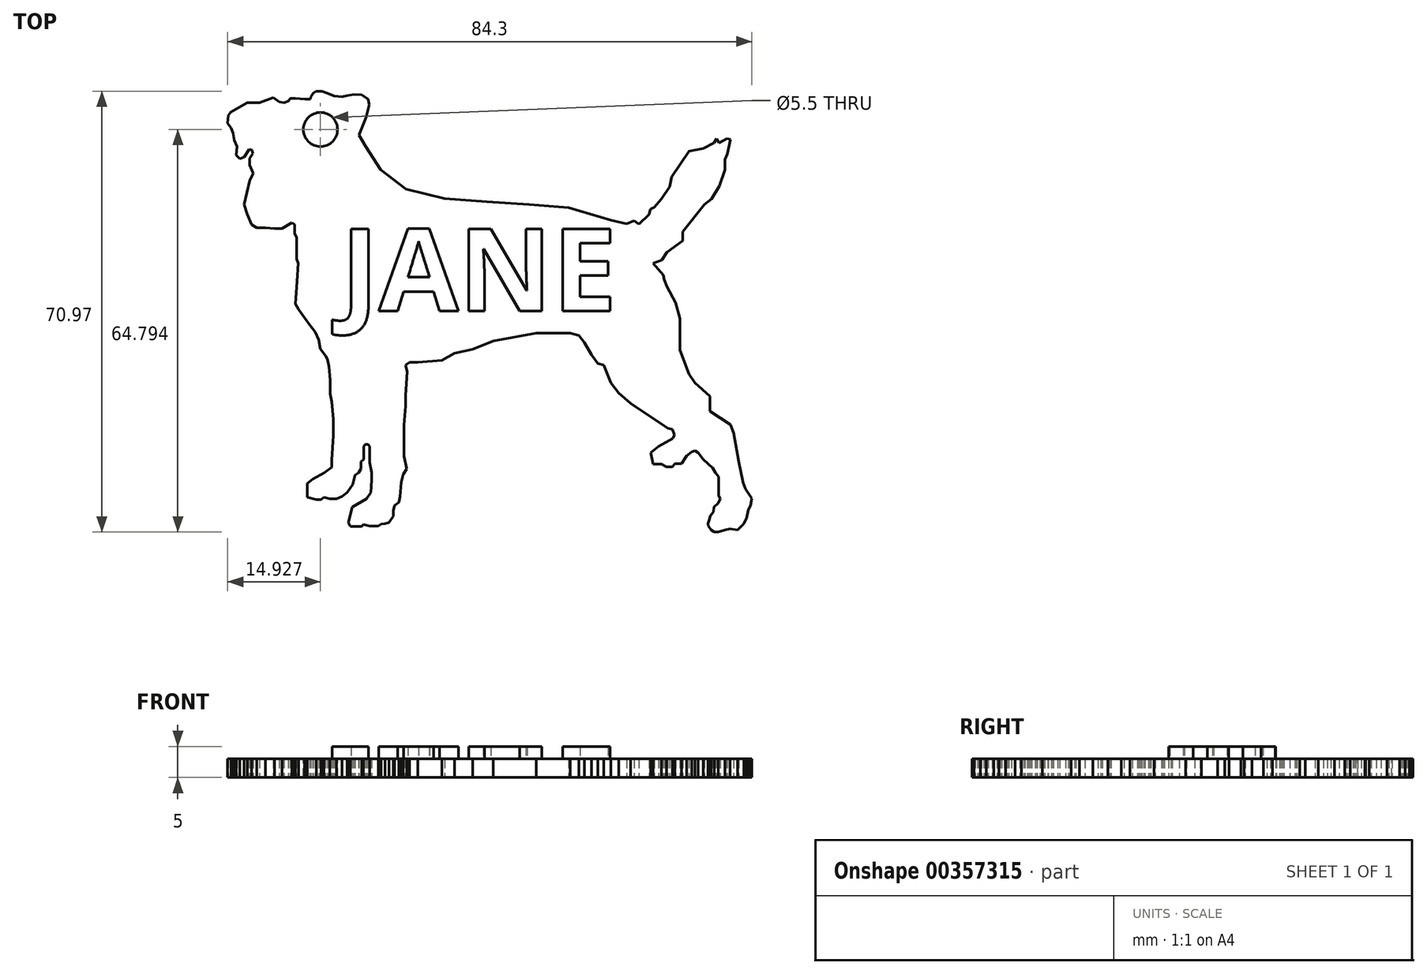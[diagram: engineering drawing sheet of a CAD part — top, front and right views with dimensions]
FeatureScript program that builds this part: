
annotation { "Feature Type Name" : "Feature", "Feature Type Description" : "" }
export const myFeature = defineFeature(function(context is Context, id is Id, definition is map)
    precondition{}
    {
        {
            var Q0;
            Q0=qCreatedBy(makeId("Top.planeOp"),FACE);
            var sketch = newSketch(context, id + "F0", { "sketchPlane" : qUnion([Q0])});
            skLineSegment(sketch, "E0", {"start": v(-3.64, 1.42) * mm, "end": v(-2.43, 1.25) * mm});
            skLineSegment(sketch, "E1", {"start": v(-2.43, 1.25) * mm, "end": v(-1.42, 2.22) * mm});
            skLineSegment(sketch, "E2", {"start": v(-1.42, 2.22) * mm, "end": v(-0.94, 3.22) * mm});
            skLineSegment(sketch, "E3", {"start": v(-0.94, 3.22) * mm, "end": v(-0.7, 4.4) * mm});
            skLineSegment(sketch, "E4", {"start": v(-0.7, 4.4) * mm, "end": v(-0.36, 5.26) * mm});
            skLineSegment(sketch, "E5", {"start": v(-0.36, 5.26) * mm, "end": v(-0.15, 6.3) * mm});
            skLineSegment(sketch, "E6", {"start": v(-0.15, 6.3) * mm, "end": v(-1.13, 7.85) * mm});
            skLineSegment(sketch, "E7", {"start": v(-1.13, 7.85) * mm, "end": v(-1.54, 8.84) * mm});
            skLineSegment(sketch, "E8", {"start": v(-1.54, 8.84) * mm, "end": v(-2.22, 12.2) * mm});
            skLineSegment(sketch, "E9", {"start": v(-2.22, 12.2) * mm, "end": v(-3.06, 16.88) * mm});
            skLineSegment(sketch, "E10", {"start": v(-3.06, 16.88) * mm, "end": v(-3.59, 18.18) * mm});
            skLineSegment(sketch, "E11", {"start": v(-3.59, 18.18) * mm, "end": v(-6.88, 20.38) * mm});
            skLineSegment(sketch, "E12", {"start": v(-6.88, 20.38) * mm, "end": v(-6.88, 22.74) * mm});
            skLineSegment(sketch, "E13", {"start": v(-6.88, 22.74) * mm, "end": v(-9.3, 24.95) * mm});
            skLineSegment(sketch, "E14", {"start": v(-9.3, 24.95) * mm, "end": v(-10.24, 26.3) * mm});
            skLineSegment(sketch, "E15", {"start": v(-10.24, 26.3) * mm, "end": v(-11.68, 30.22) * mm});
            skLineSegment(sketch, "E16", {"start": v(-11.68, 30.22) * mm, "end": v(-11.68, 35.25) * mm});
            skLineSegment(sketch, "E17", {"start": v(-11.68, 35.25) * mm, "end": v(-12.4, 37.82) * mm});
            skLineSegment(sketch, "E18", {"start": v(-12.4, 37.82) * mm, "end": v(-13.77, 40.43) * mm});
            skLineSegment(sketch, "E19", {"start": v(-13.77, 40.43) * mm, "end": v(-14.23, 41.56) * mm});
            skLineSegment(sketch, "E20", {"start": v(-14.23, 41.56) * mm, "end": v(-14.35, 42.25) * mm});
            skLineSegment(sketch, "E21", {"start": v(-14.35, 42.25) * mm, "end": v(-15.99, 44.15) * mm});
            skLineSegment(sketch, "E22", {"start": v(-15.99, 44.15) * mm, "end": v(-14.65, 44.64) * mm});
            skLineSegment(sketch, "E23", {"start": v(-14.65, 44.64) * mm, "end": v(-13.78, 45.95) * mm});
            skLineSegment(sketch, "E24", {"start": v(-13.78, 45.95) * mm, "end": v(-11.25, 47.77) * mm});
            skLineSegment(sketch, "E25", {"start": v(-11.25, 47.77) * mm, "end": v(-11.25, 49.24) * mm});
            skLineSegment(sketch, "E26", {"start": v(-11.25, 49.24) * mm, "end": v(-7.8, 53.6) * mm});
            skLineSegment(sketch, "E27", {"start": v(-7.8, 53.6) * mm, "end": v(-6.61, 54.52) * mm});
            skLineSegment(sketch, "E28", {"start": v(-6.61, 54.52) * mm, "end": v(-5.38, 56.64) * mm});
            skLineSegment(sketch, "E29", {"start": v(-5.38, 56.64) * mm, "end": v(-4.49, 59.24) * mm});
            skLineSegment(sketch, "E30", {"start": v(-4.49, 59.24) * mm, "end": v(-4.49, 60.88) * mm});
            skLineSegment(sketch, "E31", {"start": v(-4.49, 60.88) * mm, "end": v(-4.1, 61.74) * mm});
            skLineSegment(sketch, "E32", {"start": v(-4.1, 61.74) * mm, "end": v(-3.56, 64.1) * mm});
            skLineSegment(sketch, "E33", {"start": v(-3.56, 64.1) * mm, "end": v(-4.14, 64.23) * mm});
            skLineSegment(sketch, "E34", {"start": v(-4.14, 64.23) * mm, "end": v(-5.41, 63.5) * mm});
            skLineSegment(sketch, "E35", {"start": v(-5.41, 63.5) * mm, "end": v(-5.8, 64.2) * mm});
            skLineSegment(sketch, "E36", {"start": v(-5.8, 64.2) * mm, "end": v(-6.26, 63.5) * mm});
            skLineSegment(sketch, "E37", {"start": v(-6.26, 63.5) * mm, "end": v(-7.98, 62.65) * mm});
            skLineSegment(sketch, "E38", {"start": v(-7.98, 62.65) * mm, "end": v(-10.24, 62.2) * mm});
            skLineSegment(sketch, "E39", {"start": v(-10.24, 62.2) * mm, "end": v(-12.26, 59.17) * mm});
            skLineSegment(sketch, "E40", {"start": v(-12.26, 59.17) * mm, "end": v(-13, 58.05) * mm});
            skLineSegment(sketch, "E41", {"start": v(-13, 58.05) * mm, "end": v(-13.32, 56.49) * mm});
            skLineSegment(sketch, "E42", {"start": v(-13.32, 56.49) * mm, "end": v(-14.65, 54.5) * mm});
            skLineSegment(sketch, "E43", {"start": v(-14.65, 54.5) * mm, "end": v(-15.82, 53.16) * mm});
            skLineSegment(sketch, "E44", {"start": v(-15.82, 53.16) * mm, "end": v(-16.47, 52.9) * mm});
            skLineSegment(sketch, "E45", {"start": v(-16.47, 52.9) * mm, "end": v(-16.67, 52.06) * mm});
            skLineSegment(sketch, "E46", {"start": v(-16.67, 52.06) * mm, "end": v(-18.33, 50.48) * mm});
            skLineSegment(sketch, "E47", {"start": v(-18.33, 50.48) * mm, "end": v(-19.1, 51) * mm});
            skLineSegment(sketch, "E48", {"start": v(-19.1, 51) * mm, "end": v(-20.28, 50.51) * mm});
            skLineSegment(sketch, "E49", {"start": v(-20.28, 50.51) * mm, "end": v(-22.75, 51.11) * mm});
            skLineSegment(sketch, "E50", {"start": v(-22.75, 51.11) * mm, "end": v(-29.59, 53.13) * mm});
            skLineSegment(sketch, "E51", {"start": v(-29.59, 53.13) * mm, "end": v(-35.94, 53.6) * mm});
            skLineSegment(sketch, "E52", {"start": v(-35.94, 53.6) * mm, "end": v(-42.74, 54.08) * mm});
            skLineSegment(sketch, "E53", {"start": v(-42.74, 54.08) * mm, "end": v(-49.55, 54.6) * mm});
            skLineSegment(sketch, "E54", {"start": v(-49.55, 54.6) * mm, "end": v(-55.76, 56.1) * mm});
            skLineSegment(sketch, "E55", {"start": v(-55.76, 56.1) * mm, "end": v(-59.84, 59.24) * mm});
            skLineSegment(sketch, "E56", {"start": v(-59.84, 59.24) * mm, "end": v(-62.23, 62.97) * mm});
            skLineSegment(sketch, "E57", {"start": v(-62.23, 62.97) * mm, "end": v(-63.35, 64.79) * mm});
            skLineSegment(sketch, "E58", {"start": v(-63.35, 64.79) * mm, "end": v(-62.2, 67.64) * mm});
            skLineSegment(sketch, "E59", {"start": v(-62.2, 67.64) * mm, "end": v(-61.7, 69.7) * mm});
            skLineSegment(sketch, "E60", {"start": v(-61.7, 69.7) * mm, "end": v(-61.87, 70.6) * mm});
            skLineSegment(sketch, "E61", {"start": v(-61.87, 70.6) * mm, "end": v(-62.86, 71.27) * mm});
            skLineSegment(sketch, "E62", {"start": v(-62.86, 71.27) * mm, "end": v(-64.08, 71.35) * mm});
            skLineSegment(sketch, "E63", {"start": v(-64.08, 71.35) * mm, "end": v(-65.22, 71.15) * mm});
            skLineSegment(sketch, "E64", {"start": v(-65.22, 71.15) * mm, "end": v(-66.05, 70.98) * mm});
            skLineSegment(sketch, "E65", {"start": v(-66.05, 70.98) * mm, "end": v(-67.32, 71.07) * mm});
            skLineSegment(sketch, "E66", {"start": v(-67.32, 71.07) * mm, "end": v(-68.4, 71.56) * mm});
            skLineSegment(sketch, "E67", {"start": v(-68.4, 71.56) * mm, "end": v(-69.29, 71.87) * mm});
            skLineSegment(sketch, "E68", {"start": v(-69.29, 71.87) * mm, "end": v(-70.27, 71.87) * mm});
            skLineSegment(sketch, "E69", {"start": v(-70.27, 71.87) * mm, "end": v(-70.7, 71.5) * mm});
            skLineSegment(sketch, "E70", {"start": v(-70.7, 71.5) * mm, "end": v(-71.06, 70.98) * mm});
            skLineSegment(sketch, "E71", {"start": v(-71.06, 70.98) * mm, "end": v(-71.15, 70.6) * mm});
            skLineSegment(sketch, "E72", {"start": v(-71.15, 70.6) * mm, "end": v(-72.04, 70.6) * mm});
            skLineSegment(sketch, "E73", {"start": v(-72.04, 70.6) * mm, "end": v(-73.58, 70.72) * mm});
            skLineSegment(sketch, "E74", {"start": v(-73.58, 70.72) * mm, "end": v(-74.4, 70.72) * mm});
            skLineSegment(sketch, "E75", {"start": v(-74.4, 70.72) * mm, "end": v(-74.71, 70.26) * mm});
            skLineSegment(sketch, "E76", {"start": v(-74.71, 70.26) * mm, "end": v(-75.4, 69.99) * mm});
            skLineSegment(sketch, "E77", {"start": v(-75.4, 69.99) * mm, "end": v(-76.13, 70.17) * mm});
            skLineSegment(sketch, "E78", {"start": v(-76.13, 70.17) * mm, "end": v(-77.12, 70.82) * mm});
            skLineSegment(sketch, "E79", {"start": v(-77.12, 70.82) * mm, "end": v(-78.44, 70.34) * mm});
            skLineSegment(sketch, "E80", {"start": v(-78.44, 70.34) * mm, "end": v(-79.36, 70) * mm});
            skLineSegment(sketch, "E81", {"start": v(-79.36, 70) * mm, "end": v(-81.32, 70) * mm});
            skLineSegment(sketch, "E82", {"start": v(-81.32, 70) * mm, "end": v(-83.98, 68.5) * mm});
            skLineSegment(sketch, "E83", {"start": v(-83.98, 68.5) * mm, "end": v(-84.32, 67.99) * mm});
            skLineSegment(sketch, "E84", {"start": v(-84.32, 67.99) * mm, "end": v(-84.45, 66.71) * mm});
            skLineSegment(sketch, "E85", {"start": v(-84.45, 66.71) * mm, "end": v(-83.92, 65.94) * mm});
            skLineSegment(sketch, "E86", {"start": v(-83.92, 65.94) * mm, "end": v(-83.61, 65.1) * mm});
            skLineSegment(sketch, "E87", {"start": v(-83.61, 65.1) * mm, "end": v(-83.39, 64) * mm});
            skLineSegment(sketch, "E88", {"start": v(-83.39, 64) * mm, "end": v(-82.97, 62.97) * mm});
            skLineSegment(sketch, "E89", {"start": v(-82.97, 62.97) * mm, "end": v(-83.07, 61.56) * mm});
            skLineSegment(sketch, "E90", {"start": v(-83.07, 61.56) * mm, "end": v(-82.5, 60.97) * mm});
            skLineSegment(sketch, "E91", {"start": v(-82.5, 60.97) * mm, "end": v(-81.81, 61.24) * mm});
            skLineSegment(sketch, "E92", {"start": v(-81.81, 61.24) * mm, "end": v(-81.33, 61.97) * mm});
            skLineSegment(sketch, "E93", {"start": v(-81.33, 61.97) * mm, "end": v(-80.97, 62.52) * mm});
            skLineSegment(sketch, "E94", {"start": v(-80.97, 62.52) * mm, "end": v(-80.5, 62.4) * mm});
            skLineSegment(sketch, "E95", {"start": v(-80.5, 62.4) * mm, "end": v(-80.38, 61.8) * mm});
            skLineSegment(sketch, "E96", {"start": v(-80.38, 61.8) * mm, "end": v(-80.9, 61.03) * mm});
            skLineSegment(sketch, "E97", {"start": v(-80.9, 61.03) * mm, "end": v(-80.9, 59.97) * mm});
            skLineSegment(sketch, "E98", {"start": v(-80.9, 59.97) * mm, "end": v(-80.36, 58.63) * mm});
            skLineSegment(sketch, "E99", {"start": v(-80.36, 58.63) * mm, "end": v(-80.9, 57.45) * mm});
            skLineSegment(sketch, "E100", {"start": v(-80.9, 57.45) * mm, "end": v(-81.32, 55.75) * mm});
            skLineSegment(sketch, "E101", {"start": v(-81.32, 55.75) * mm, "end": v(-81.83, 53.6) * mm});
            skLineSegment(sketch, "E102", {"start": v(-81.83, 53.6) * mm, "end": v(-81.27, 52.06) * mm});
            skLineSegment(sketch, "E103", {"start": v(-81.27, 52.06) * mm, "end": v(-80.6, 50.4) * mm});
            skLineSegment(sketch, "E104", {"start": v(-80.6, 50.4) * mm, "end": v(-79.8, 49.86) * mm});
            skLineSegment(sketch, "E105", {"start": v(-79.8, 49.86) * mm, "end": v(-78.37, 49.86) * mm});
            skLineSegment(sketch, "E106", {"start": v(-78.37, 49.86) * mm, "end": v(-76.93, 49.76) * mm});
            skLineSegment(sketch, "E107", {"start": v(-76.93, 49.76) * mm, "end": v(-75.74, 49.76) * mm});
            skLineSegment(sketch, "E108", {"start": v(-75.74, 49.76) * mm, "end": v(-74.9, 50.24) * mm});
            skLineSegment(sketch, "E109", {"start": v(-74.9, 50.24) * mm, "end": v(-74.11, 50.68) * mm});
            skLineSegment(sketch, "E110", {"start": v(-74.11, 50.68) * mm, "end": v(-73.68, 50.4) * mm});
            skLineSegment(sketch, "E111", {"start": v(-73.68, 50.4) * mm, "end": v(-73.68, 48.9) * mm});
            skLineSegment(sketch, "E112", {"start": v(-73.68, 48.9) * mm, "end": v(-73.38, 48.38) * mm});
            skLineSegment(sketch, "E113", {"start": v(-73.38, 48.38) * mm, "end": v(-73.38, 44.89) * mm});
            skLineSegment(sketch, "E114", {"start": v(-73.38, 44.89) * mm, "end": v(-73.09, 44.17) * mm});
            skLineSegment(sketch, "E115", {"start": v(-73.09, 44.17) * mm, "end": v(-73.3, 41.23) * mm});
            skLineSegment(sketch, "E116", {"start": v(-73.3, 41.23) * mm, "end": v(-73.57, 37.63) * mm});
            skLineSegment(sketch, "E117", {"start": v(-73.57, 37.63) * mm, "end": v(-73.05, 36.72) * mm});
            skLineSegment(sketch, "E118", {"start": v(-73.05, 36.72) * mm, "end": v(-72.1, 35.37) * mm});
            skLineSegment(sketch, "E119", {"start": v(-72.1, 35.37) * mm, "end": v(-71.25, 34.24) * mm});
            skLineSegment(sketch, "E120", {"start": v(-71.25, 34.24) * mm, "end": v(-70.35, 33.14) * mm});
            skLineSegment(sketch, "E121", {"start": v(-70.35, 33.14) * mm, "end": v(-69.83, 31.85) * mm});
            skLineSegment(sketch, "E122", {"start": v(-69.83, 31.85) * mm, "end": v(-69.53, 30.4) * mm});
            skLineSegment(sketch, "E123", {"start": v(-69.53, 30.4) * mm, "end": v(-68.74, 29.32) * mm});
            skLineSegment(sketch, "E124", {"start": v(-68.74, 29.32) * mm, "end": v(-68.4, 28.71) * mm});
            skLineSegment(sketch, "E125", {"start": v(-68.4, 28.71) * mm, "end": v(-68.15, 27.5) * mm});
            skLineSegment(sketch, "E126", {"start": v(-68.15, 27.5) * mm, "end": v(-67.95, 25.36) * mm});
            skLineSegment(sketch, "E127", {"start": v(-67.95, 25.36) * mm, "end": v(-67.95, 23.15) * mm});
            skLineSegment(sketch, "E128", {"start": v(-67.95, 23.15) * mm, "end": v(-67.69, 21.87) * mm});
            skLineSegment(sketch, "E129", {"start": v(-67.69, 21.87) * mm, "end": v(-67.47, 19.06) * mm});
            skLineSegment(sketch, "E130", {"start": v(-67.47, 19.06) * mm, "end": v(-67.47, 16.4) * mm});
            skLineSegment(sketch, "E131", {"start": v(-67.47, 16.4) * mm, "end": v(-67.59, 14.67) * mm});
            skLineSegment(sketch, "E132", {"start": v(-67.59, 14.67) * mm, "end": v(-67.74, 12.53) * mm});
            skLineSegment(sketch, "E133", {"start": v(-67.74, 12.53) * mm, "end": v(-67.74, 11.33) * mm});
            skLineSegment(sketch, "E134", {"start": v(-67.74, 11.33) * mm, "end": v(-68.93, 10.43) * mm});
            skLineSegment(sketch, "E135", {"start": v(-68.93, 10.43) * mm, "end": v(-70.73, 9.4) * mm});
            skLineSegment(sketch, "E136", {"start": v(-70.73, 9.4) * mm, "end": v(-71.64, 8.72) * mm});
            skLineSegment(sketch, "E137", {"start": v(-71.64, 8.72) * mm, "end": v(-71.64, 6.5) * mm});
            skLineSegment(sketch, "E138", {"start": v(-71.64, 6.5) * mm, "end": v(-70.19, 6.14) * mm});
            skLineSegment(sketch, "E139", {"start": v(-70.19, 6.14) * mm, "end": v(-69.45, 6.14) * mm});
            skLineSegment(sketch, "E140", {"start": v(-69.45, 6.14) * mm, "end": v(-69, 6.49) * mm});
            skLineSegment(sketch, "E141", {"start": v(-69, 6.49) * mm, "end": v(-68.05, 6.26) * mm});
            skLineSegment(sketch, "E142", {"start": v(-68.05, 6.26) * mm, "end": v(-67.59, 6.26) * mm});
            skLineSegment(sketch, "E143", {"start": v(-67.59, 6.26) * mm, "end": v(-66.97, 6.26) * mm});
            skLineSegment(sketch, "E144", {"start": v(-66.97, 6.26) * mm, "end": v(-66.05, 6.63) * mm});
            skLineSegment(sketch, "E145", {"start": v(-66.05, 6.63) * mm, "end": v(-65.23, 7.24) * mm});
            skLineSegment(sketch, "E146", {"start": v(-65.23, 7.24) * mm, "end": v(-64.83, 7.85) * mm});
            skLineSegment(sketch, "E147", {"start": v(-64.83, 7.85) * mm, "end": v(-64.35, 8.57) * mm});
            skLineSegment(sketch, "E148", {"start": v(-64.35, 8.57) * mm, "end": v(-64, 10.04) * mm});
            skLineSegment(sketch, "E149", {"start": v(-64, 10.04) * mm, "end": v(-63.42, 10.48) * mm});
            skLineSegment(sketch, "E150", {"start": v(-63.42, 10.48) * mm, "end": v(-63.03, 11.07) * mm});
            skLineSegment(sketch, "E151", {"start": v(-63.03, 11.07) * mm, "end": v(-63.03, 12.23) * mm});
            skLineSegment(sketch, "E152", {"start": v(-63.03, 12.23) * mm, "end": v(-62.56, 12.57) * mm});
            skLineSegment(sketch, "E153", {"start": v(-62.56, 12.57) * mm, "end": v(-62.56, 14.67) * mm});
            skLineSegment(sketch, "E154", {"start": v(-62.56, 14.67) * mm, "end": v(-62.33, 15.02) * mm});
            skLineSegment(sketch, "E155", {"start": v(-62.33, 15.02) * mm, "end": v(-61.87, 15.02) * mm});
            skLineSegment(sketch, "E156", {"start": v(-61.87, 15.02) * mm, "end": v(-61.6, 14.67) * mm});
            skLineSegment(sketch, "E157", {"start": v(-61.6, 14.67) * mm, "end": v(-61.6, 12.1) * mm});
            skLineSegment(sketch, "E158", {"start": v(-61.6, 12.1) * mm, "end": v(-61.28, 10.52) * mm});
            skLineSegment(sketch, "E159", {"start": v(-61.28, 10.52) * mm, "end": v(-61.28, 9.27) * mm});
            skLineSegment(sketch, "E160", {"start": v(-61.28, 9.27) * mm, "end": v(-61.33, 8.6) * mm});
            skLineSegment(sketch, "E161", {"start": v(-61.33, 8.6) * mm, "end": v(-61.42, 7.28) * mm});
            skLineSegment(sketch, "E162", {"start": v(-61.42, 7.28) * mm, "end": v(-62.11, 6.24) * mm});
            skLineSegment(sketch, "E163", {"start": v(-62.11, 6.24) * mm, "end": v(-64.43, 4.93) * mm});
            skLineSegment(sketch, "E164", {"start": v(-64.43, 4.93) * mm, "end": v(-65.03, 2.46) * mm});
            skLineSegment(sketch, "E165", {"start": v(-65.03, 2.46) * mm, "end": v(-64.76, 1.78) * mm});
            skLineSegment(sketch, "E166", {"start": v(-64.76, 1.78) * mm, "end": v(-63.8, 1.78) * mm});
            skLineSegment(sketch, "E167", {"start": v(-63.8, 1.78) * mm, "end": v(-62.86, 1.78) * mm});
            skLineSegment(sketch, "E168", {"start": v(-62.86, 1.78) * mm, "end": v(-62.63, 2.11) * mm});
            skLineSegment(sketch, "E169", {"start": v(-62.63, 2.11) * mm, "end": v(-61.61, 1.87) * mm});
            skLineSegment(sketch, "E170", {"start": v(-61.61, 1.87) * mm, "end": v(-60.22, 1.87) * mm});
            skLineSegment(sketch, "E171", {"start": v(-60.22, 1.87) * mm, "end": v(-59.77, 2.2) * mm});
            skLineSegment(sketch, "E172", {"start": v(-59.77, 2.2) * mm, "end": v(-59.16, 2.24) * mm});
            skLineSegment(sketch, "E173", {"start": v(-59.16, 2.24) * mm, "end": v(-58.48, 2.46) * mm});
            skLineSegment(sketch, "E174", {"start": v(-58.48, 2.46) * mm, "end": v(-57.82, 3.43) * mm});
            skLineSegment(sketch, "E175", {"start": v(-57.82, 3.43) * mm, "end": v(-57.82, 4.32) * mm});
            skLineSegment(sketch, "E176", {"start": v(-57.82, 4.32) * mm, "end": v(-57.62, 5.18) * mm});
            skLineSegment(sketch, "E177", {"start": v(-57.62, 5.18) * mm, "end": v(-56.93, 5.7) * mm});
            skLineSegment(sketch, "E178", {"start": v(-56.93, 5.7) * mm, "end": v(-56.7, 6.63) * mm});
            skLineSegment(sketch, "E179", {"start": v(-56.7, 6.63) * mm, "end": v(-56.54, 8.92) * mm});
            skLineSegment(sketch, "E180", {"start": v(-56.54, 8.92) * mm, "end": v(-56.23, 10.2) * mm});
            skLineSegment(sketch, "E181", {"start": v(-56.23, 10.2) * mm, "end": v(-55.66, 11.05) * mm});
            skLineSegment(sketch, "E182", {"start": v(-55.66, 11.05) * mm, "end": v(-56.08, 13.12) * mm});
            skLineSegment(sketch, "E183", {"start": v(-56.08, 13.12) * mm, "end": v(-56.08, 15.04) * mm});
            skLineSegment(sketch, "E184", {"start": v(-56.08, 15.04) * mm, "end": v(-56.08, 18.1) * mm});
            skLineSegment(sketch, "E185", {"start": v(-56.08, 18.1) * mm, "end": v(-55.86, 21.18) * mm});
            skLineSegment(sketch, "E186", {"start": v(-55.86, 21.18) * mm, "end": v(-55.86, 22.91) * mm});
            skLineSegment(sketch, "E187", {"start": v(-55.86, 22.91) * mm, "end": v(-55.6, 26.72) * mm});
            skLineSegment(sketch, "E188", {"start": v(-55.6, 26.72) * mm, "end": v(-55.8, 27.77) * mm});
            skLineSegment(sketch, "E189", {"start": v(-55.8, 27.77) * mm, "end": v(-55.17, 28.25) * mm});
            skLineSegment(sketch, "E190", {"start": v(-55.17, 28.25) * mm, "end": v(-53.84, 28.25) * mm});
            skLineSegment(sketch, "E191", {"start": v(-53.84, 28.25) * mm, "end": v(-50.02, 28.55) * mm});
            skLineSegment(sketch, "E192", {"start": v(-50.02, 28.55) * mm, "end": v(-47.97, 29.71) * mm});
            skLineSegment(sketch, "E193", {"start": v(-47.97, 29.71) * mm, "end": v(-45.05, 30.3) * mm});
            skLineSegment(sketch, "E194", {"start": v(-45.05, 30.3) * mm, "end": v(-41.73, 31.65) * mm});
            skLineSegment(sketch, "E195", {"start": v(-41.73, 31.65) * mm, "end": v(-34.8, 32.9) * mm});
            skLineSegment(sketch, "E196", {"start": v(-34.8, 32.9) * mm, "end": v(-31.16, 32.9) * mm});
            skLineSegment(sketch, "E197", {"start": v(-31.16, 32.9) * mm, "end": v(-29.39, 32.9) * mm});
            skLineSegment(sketch, "E198", {"start": v(-29.39, 32.9) * mm, "end": v(-27.95, 32.55) * mm});
            skLineSegment(sketch, "E199", {"start": v(-27.95, 32.55) * mm, "end": v(-27.06, 31.37) * mm});
            skLineSegment(sketch, "E200", {"start": v(-27.06, 31.37) * mm, "end": v(-25.94, 29.4) * mm});
            skLineSegment(sketch, "E201", {"start": v(-25.94, 29.4) * mm, "end": v(-24.9, 28.03) * mm});
            skLineSegment(sketch, "E202", {"start": v(-24.9, 28.03) * mm, "end": v(-23.96, 27.8) * mm});
            skLineSegment(sketch, "E203", {"start": v(-23.96, 27.8) * mm, "end": v(-22.8, 24.95) * mm});
            skLineSegment(sketch, "E204", {"start": v(-22.8, 24.95) * mm, "end": v(-21.53, 23.27) * mm});
            skLineSegment(sketch, "E205", {"start": v(-21.53, 23.27) * mm, "end": v(-19.65, 21.62) * mm});
            skLineSegment(sketch, "E206", {"start": v(-19.65, 21.62) * mm, "end": v(-17.49, 20.18) * mm});
            skLineSegment(sketch, "E207", {"start": v(-17.49, 20.18) * mm, "end": v(-15.67, 18.96) * mm});
            skLineSegment(sketch, "E208", {"start": v(-15.67, 18.96) * mm, "end": v(-13.68, 17.63) * mm});
            skLineSegment(sketch, "E209", {"start": v(-13.68, 17.63) * mm, "end": v(-12.91, 17.45) * mm});
            skLineSegment(sketch, "E210", {"start": v(-12.91, 17.45) * mm, "end": v(-12.57, 16.51) * mm});
            skLineSegment(sketch, "E211", {"start": v(-12.57, 16.51) * mm, "end": v(-12.83, 15.98) * mm});
            skLineSegment(sketch, "E212", {"start": v(-12.83, 15.98) * mm, "end": v(-14.02, 15.3) * mm});
            skLineSegment(sketch, "E213", {"start": v(-14.02, 15.3) * mm, "end": v(-15.14, 14.67) * mm});
            skLineSegment(sketch, "E214", {"start": v(-15.14, 14.67) * mm, "end": v(-16.42, 13.7) * mm});
            skLineSegment(sketch, "E215", {"start": v(-16.42, 13.7) * mm, "end": v(-16.04, 11.83) * mm});
            skLineSegment(sketch, "E216", {"start": v(-16.04, 11.83) * mm, "end": v(-15.17, 11.83) * mm});
            skLineSegment(sketch, "E217", {"start": v(-15.17, 11.83) * mm, "end": v(-14.65, 11.83) * mm});
            skLineSegment(sketch, "E218", {"start": v(-14.65, 11.83) * mm, "end": v(-13.85, 11.39) * mm});
            skLineSegment(sketch, "E219", {"start": v(-13.85, 11.39) * mm, "end": v(-12.9, 11.39) * mm});
            skLineSegment(sketch, "E220", {"start": v(-12.9, 11.39) * mm, "end": v(-12.53, 11.94) * mm});
            skLineSegment(sketch, "E221", {"start": v(-12.53, 11.94) * mm, "end": v(-11.47, 11.91) * mm});
            skLineSegment(sketch, "E222", {"start": v(-11.47, 11.91) * mm, "end": v(-10.62, 13.2) * mm});
            skLineSegment(sketch, "E223", {"start": v(-10.62, 13.2) * mm, "end": v(-9.81, 13.8) * mm});
            skLineSegment(sketch, "E224", {"start": v(-9.81, 13.8) * mm, "end": v(-9.3, 14.03) * mm});
            skLineSegment(sketch, "E225", {"start": v(-9.3, 14.03) * mm, "end": v(-8.8, 13.7) * mm});
            skLineSegment(sketch, "E226", {"start": v(-8.8, 13.7) * mm, "end": v(-7.96, 12.57) * mm});
            skLineSegment(sketch, "E227", {"start": v(-7.96, 12.57) * mm, "end": v(-6.4, 11.23) * mm});
            skLineSegment(sketch, "E228", {"start": v(-6.4, 11.23) * mm, "end": v(-5.97, 10.47) * mm});
            skLineSegment(sketch, "E229", {"start": v(-5.97, 10.47) * mm, "end": v(-5.46, 9.8) * mm});
            skLineSegment(sketch, "E230", {"start": v(-5.46, 9.8) * mm, "end": v(-5.46, 8.22) * mm});
            skLineSegment(sketch, "E231", {"start": v(-5.46, 8.22) * mm, "end": v(-5.46, 6.84) * mm});
            skLineSegment(sketch, "E232", {"start": v(-5.46, 6.84) * mm, "end": v(-5.22, 6.25) * mm});
            skLineSegment(sketch, "E233", {"start": v(-5.22, 6.25) * mm, "end": v(-5.55, 5.57) * mm});
            skLineSegment(sketch, "E234", {"start": v(-5.55, 5.57) * mm, "end": v(-6.24, 4.93) * mm});
            skLineSegment(sketch, "E235", {"start": v(-6.24, 4.93) * mm, "end": v(-6.29, 4.16) * mm});
            skLineSegment(sketch, "E236", {"start": v(-6.29, 4.16) * mm, "end": v(-6.82, 3.52) * mm});
            skLineSegment(sketch, "E237", {"start": v(-6.82, 3.52) * mm, "end": v(-7.02, 2.8) * mm});
            skLineSegment(sketch, "E238", {"start": v(-7.02, 2.8) * mm, "end": v(-7.2, 2.25) * mm});
            skLineSegment(sketch, "E239", {"start": v(-7.2, 2.25) * mm, "end": v(-7.16, 1.87) * mm});
            skLineSegment(sketch, "E240", {"start": v(-7.16, 1.87) * mm, "end": v(-6.68, 1.25) * mm});
            skLineSegment(sketch, "E241", {"start": v(-6.68, 1.25) * mm, "end": v(-6.17, 0.9) * mm});
            skLineSegment(sketch, "E242", {"start": v(-6.17, 0.9) * mm, "end": v(-5.57, 0.93) * mm});
            skLineSegment(sketch, "E243", {"start": v(-5.57, 0.93) * mm, "end": v(-4.49, 1.25) * mm});
            skLineSegment(sketch, "E244", {"start": v(-4.49, 1.25) * mm, "end": v(-3.64, 1.42) * mm});
            skSolve(sketch);
        }
        {
            var Q0;
            Q0=makeQuery(id+"F0.imprint","IMPRINT",FACE,{"disambiguationData":[TD([[makeQuery(id+"F0.imprint","IMPRINT",EDGE,{"derivedFrom":sQuery(id+"F0.wireOp",EDGE,"E0")}),1.0]])]});
            extrude(context, id + "F1", {"entities" : qUnion([Q0]), "depth" : 3 * mm});
        }
        {
            var Q0;
            Q0=makeQuery(id+"F1.opExtrude","CAP_FACE",FACE,{"disambiguationData":[OSD([sQuery(id+"F0.wireOp",EDGE,"E0"),sQuery(id+"F0.wireOp",EDGE,"E1"),sQuery(id+"F0.wireOp",EDGE,"E2"),sQuery(id+"F0.wireOp",EDGE,"E3"),sQuery(id+"F0.wireOp",EDGE,"E4"),sQuery(id+"F0.wireOp",EDGE,"E5"),sQuery(id+"F0.wireOp",EDGE,"E6"),sQuery(id+"F0.wireOp",EDGE,"E7"),sQuery(id+"F0.wireOp",EDGE,"E8"),sQuery(id+"F0.wireOp",EDGE,"E9"),sQuery(id+"F0.wireOp",EDGE,"E10"),sQuery(id+"F0.wireOp",EDGE,"E11"),sQuery(id+"F0.wireOp",EDGE,"E12"),sQuery(id+"F0.wireOp",EDGE,"E13"),sQuery(id+"F0.wireOp",EDGE,"E14"),sQuery(id+"F0.wireOp",EDGE,"E15"),sQuery(id+"F0.wireOp",EDGE,"E16"),sQuery(id+"F0.wireOp",EDGE,"E17"),sQuery(id+"F0.wireOp",EDGE,"E18"),sQuery(id+"F0.wireOp",EDGE,"E19"),sQuery(id+"F0.wireOp",EDGE,"E20"),sQuery(id+"F0.wireOp",EDGE,"E21"),sQuery(id+"F0.wireOp",EDGE,"E22"),sQuery(id+"F0.wireOp",EDGE,"E23"),sQuery(id+"F0.wireOp",EDGE,"E24"),sQuery(id+"F0.wireOp",EDGE,"E25"),sQuery(id+"F0.wireOp",EDGE,"E26"),sQuery(id+"F0.wireOp",EDGE,"E27"),sQuery(id+"F0.wireOp",EDGE,"E28"),sQuery(id+"F0.wireOp",EDGE,"E29"),sQuery(id+"F0.wireOp",EDGE,"E30"),sQuery(id+"F0.wireOp",EDGE,"E31"),sQuery(id+"F0.wireOp",EDGE,"E32"),sQuery(id+"F0.wireOp",EDGE,"E33"),sQuery(id+"F0.wireOp",EDGE,"E34"),sQuery(id+"F0.wireOp",EDGE,"E35"),sQuery(id+"F0.wireOp",EDGE,"E36"),sQuery(id+"F0.wireOp",EDGE,"E37"),sQuery(id+"F0.wireOp",EDGE,"E38"),sQuery(id+"F0.wireOp",EDGE,"E39"),sQuery(id+"F0.wireOp",EDGE,"E40"),sQuery(id+"F0.wireOp",EDGE,"E41"),sQuery(id+"F0.wireOp",EDGE,"E42"),sQuery(id+"F0.wireOp",EDGE,"E43"),sQuery(id+"F0.wireOp",EDGE,"E44"),sQuery(id+"F0.wireOp",EDGE,"E45"),sQuery(id+"F0.wireOp",EDGE,"E46"),sQuery(id+"F0.wireOp",EDGE,"E47"),sQuery(id+"F0.wireOp",EDGE,"E48"),sQuery(id+"F0.wireOp",EDGE,"E49"),sQuery(id+"F0.wireOp",EDGE,"E50"),sQuery(id+"F0.wireOp",EDGE,"E51"),sQuery(id+"F0.wireOp",EDGE,"E52"),sQuery(id+"F0.wireOp",EDGE,"E53"),sQuery(id+"F0.wireOp",EDGE,"E54"),sQuery(id+"F0.wireOp",EDGE,"E55"),sQuery(id+"F0.wireOp",EDGE,"E56"),sQuery(id+"F0.wireOp",EDGE,"E57"),sQuery(id+"F0.wireOp",EDGE,"E58"),sQuery(id+"F0.wireOp",EDGE,"E59"),sQuery(id+"F0.wireOp",EDGE,"E60"),sQuery(id+"F0.wireOp",EDGE,"E61"),sQuery(id+"F0.wireOp",EDGE,"E62"),sQuery(id+"F0.wireOp",EDGE,"E63"),sQuery(id+"F0.wireOp",EDGE,"E64"),sQuery(id+"F0.wireOp",EDGE,"E65"),sQuery(id+"F0.wireOp",EDGE,"E66"),sQuery(id+"F0.wireOp",EDGE,"E67"),sQuery(id+"F0.wireOp",EDGE,"E68"),sQuery(id+"F0.wireOp",EDGE,"E69"),sQuery(id+"F0.wireOp",EDGE,"E70"),sQuery(id+"F0.wireOp",EDGE,"E71"),sQuery(id+"F0.wireOp",EDGE,"E72"),sQuery(id+"F0.wireOp",EDGE,"E73"),sQuery(id+"F0.wireOp",EDGE,"E74"),sQuery(id+"F0.wireOp",EDGE,"E75"),sQuery(id+"F0.wireOp",EDGE,"E76"),sQuery(id+"F0.wireOp",EDGE,"E77"),sQuery(id+"F0.wireOp",EDGE,"E78"),sQuery(id+"F0.wireOp",EDGE,"E79"),sQuery(id+"F0.wireOp",EDGE,"E80"),sQuery(id+"F0.wireOp",EDGE,"E81"),sQuery(id+"F0.wireOp",EDGE,"E82"),sQuery(id+"F0.wireOp",EDGE,"E83"),sQuery(id+"F0.wireOp",EDGE,"E84"),sQuery(id+"F0.wireOp",EDGE,"E85"),sQuery(id+"F0.wireOp",EDGE,"E86"),sQuery(id+"F0.wireOp",EDGE,"E87"),sQuery(id+"F0.wireOp",EDGE,"E88"),sQuery(id+"F0.wireOp",EDGE,"E89"),sQuery(id+"F0.wireOp",EDGE,"E90"),sQuery(id+"F0.wireOp",EDGE,"E91"),sQuery(id+"F0.wireOp",EDGE,"E92"),sQuery(id+"F0.wireOp",EDGE,"E93"),sQuery(id+"F0.wireOp",EDGE,"E94"),sQuery(id+"F0.wireOp",EDGE,"E95"),sQuery(id+"F0.wireOp",EDGE,"E96"),sQuery(id+"F0.wireOp",EDGE,"E97"),sQuery(id+"F0.wireOp",EDGE,"E98"),sQuery(id+"F0.wireOp",EDGE,"E99"),sQuery(id+"F0.wireOp",EDGE,"E100"),sQuery(id+"F0.wireOp",EDGE,"E101"),sQuery(id+"F0.wireOp",EDGE,"E102"),sQuery(id+"F0.wireOp",EDGE,"E103"),sQuery(id+"F0.wireOp",EDGE,"E104"),sQuery(id+"F0.wireOp",EDGE,"E105"),sQuery(id+"F0.wireOp",EDGE,"E106"),sQuery(id+"F0.wireOp",EDGE,"E107"),sQuery(id+"F0.wireOp",EDGE,"E108"),sQuery(id+"F0.wireOp",EDGE,"E109"),sQuery(id+"F0.wireOp",EDGE,"E110"),sQuery(id+"F0.wireOp",EDGE,"E111"),sQuery(id+"F0.wireOp",EDGE,"E112"),sQuery(id+"F0.wireOp",EDGE,"E113"),sQuery(id+"F0.wireOp",EDGE,"E114"),sQuery(id+"F0.wireOp",EDGE,"E115"),sQuery(id+"F0.wireOp",EDGE,"E116"),sQuery(id+"F0.wireOp",EDGE,"E117"),sQuery(id+"F0.wireOp",EDGE,"E118"),sQuery(id+"F0.wireOp",EDGE,"E119"),sQuery(id+"F0.wireOp",EDGE,"E120"),sQuery(id+"F0.wireOp",EDGE,"E121"),sQuery(id+"F0.wireOp",EDGE,"E122"),sQuery(id+"F0.wireOp",EDGE,"E123"),sQuery(id+"F0.wireOp",EDGE,"E124"),sQuery(id+"F0.wireOp",EDGE,"E125"),sQuery(id+"F0.wireOp",EDGE,"E126"),sQuery(id+"F0.wireOp",EDGE,"E127"),sQuery(id+"F0.wireOp",EDGE,"E128"),sQuery(id+"F0.wireOp",EDGE,"E129"),sQuery(id+"F0.wireOp",EDGE,"E130"),sQuery(id+"F0.wireOp",EDGE,"E131"),sQuery(id+"F0.wireOp",EDGE,"E132"),sQuery(id+"F0.wireOp",EDGE,"E133"),sQuery(id+"F0.wireOp",EDGE,"E134"),sQuery(id+"F0.wireOp",EDGE,"E135"),sQuery(id+"F0.wireOp",EDGE,"E136"),sQuery(id+"F0.wireOp",EDGE,"E137"),sQuery(id+"F0.wireOp",EDGE,"E138"),sQuery(id+"F0.wireOp",EDGE,"E139"),sQuery(id+"F0.wireOp",EDGE,"E140"),sQuery(id+"F0.wireOp",EDGE,"E141"),sQuery(id+"F0.wireOp",EDGE,"E142"),sQuery(id+"F0.wireOp",EDGE,"E143"),sQuery(id+"F0.wireOp",EDGE,"E144"),sQuery(id+"F0.wireOp",EDGE,"E145"),sQuery(id+"F0.wireOp",EDGE,"E146"),sQuery(id+"F0.wireOp",EDGE,"E147"),sQuery(id+"F0.wireOp",EDGE,"E148"),sQuery(id+"F0.wireOp",EDGE,"E149"),sQuery(id+"F0.wireOp",EDGE,"E150"),sQuery(id+"F0.wireOp",EDGE,"E151"),sQuery(id+"F0.wireOp",EDGE,"E152"),sQuery(id+"F0.wireOp",EDGE,"E153"),sQuery(id+"F0.wireOp",EDGE,"E154"),sQuery(id+"F0.wireOp",EDGE,"E155"),sQuery(id+"F0.wireOp",EDGE,"E156"),sQuery(id+"F0.wireOp",EDGE,"E157"),sQuery(id+"F0.wireOp",EDGE,"E158"),sQuery(id+"F0.wireOp",EDGE,"E159"),sQuery(id+"F0.wireOp",EDGE,"E160"),sQuery(id+"F0.wireOp",EDGE,"E161"),sQuery(id+"F0.wireOp",EDGE,"E162"),sQuery(id+"F0.wireOp",EDGE,"E163"),sQuery(id+"F0.wireOp",EDGE,"E164"),sQuery(id+"F0.wireOp",EDGE,"E165"),sQuery(id+"F0.wireOp",EDGE,"E166"),sQuery(id+"F0.wireOp",EDGE,"E167"),sQuery(id+"F0.wireOp",EDGE,"E168"),sQuery(id+"F0.wireOp",EDGE,"E169"),sQuery(id+"F0.wireOp",EDGE,"E170"),sQuery(id+"F0.wireOp",EDGE,"E171"),sQuery(id+"F0.wireOp",EDGE,"E172"),sQuery(id+"F0.wireOp",EDGE,"E173"),sQuery(id+"F0.wireOp",EDGE,"E174"),sQuery(id+"F0.wireOp",EDGE,"E175"),sQuery(id+"F0.wireOp",EDGE,"E176"),sQuery(id+"F0.wireOp",EDGE,"E177"),sQuery(id+"F0.wireOp",EDGE,"E178"),sQuery(id+"F0.wireOp",EDGE,"E179"),sQuery(id+"F0.wireOp",EDGE,"E180"),sQuery(id+"F0.wireOp",EDGE,"E181"),sQuery(id+"F0.wireOp",EDGE,"E182"),sQuery(id+"F0.wireOp",EDGE,"E183"),sQuery(id+"F0.wireOp",EDGE,"E184"),sQuery(id+"F0.wireOp",EDGE,"E185"),sQuery(id+"F0.wireOp",EDGE,"E186"),sQuery(id+"F0.wireOp",EDGE,"E187"),sQuery(id+"F0.wireOp",EDGE,"E188"),sQuery(id+"F0.wireOp",EDGE,"E189"),sQuery(id+"F0.wireOp",EDGE,"E190"),sQuery(id+"F0.wireOp",EDGE,"E191"),sQuery(id+"F0.wireOp",EDGE,"E192"),sQuery(id+"F0.wireOp",EDGE,"E193"),sQuery(id+"F0.wireOp",EDGE,"E194"),sQuery(id+"F0.wireOp",EDGE,"E195"),sQuery(id+"F0.wireOp",EDGE,"E196"),sQuery(id+"F0.wireOp",EDGE,"E197"),sQuery(id+"F0.wireOp",EDGE,"E198"),sQuery(id+"F0.wireOp",EDGE,"E199"),sQuery(id+"F0.wireOp",EDGE,"E200"),sQuery(id+"F0.wireOp",EDGE,"E201"),sQuery(id+"F0.wireOp",EDGE,"E202"),sQuery(id+"F0.wireOp",EDGE,"E203"),sQuery(id+"F0.wireOp",EDGE,"E204"),sQuery(id+"F0.wireOp",EDGE,"E205"),sQuery(id+"F0.wireOp",EDGE,"E206"),sQuery(id+"F0.wireOp",EDGE,"E207"),sQuery(id+"F0.wireOp",EDGE,"E208"),sQuery(id+"F0.wireOp",EDGE,"E209"),sQuery(id+"F0.wireOp",EDGE,"E210"),sQuery(id+"F0.wireOp",EDGE,"E211"),sQuery(id+"F0.wireOp",EDGE,"E212"),sQuery(id+"F0.wireOp",EDGE,"E213"),sQuery(id+"F0.wireOp",EDGE,"E214"),sQuery(id+"F0.wireOp",EDGE,"E215"),sQuery(id+"F0.wireOp",EDGE,"E216"),sQuery(id+"F0.wireOp",EDGE,"E217"),sQuery(id+"F0.wireOp",EDGE,"E218"),sQuery(id+"F0.wireOp",EDGE,"E219"),sQuery(id+"F0.wireOp",EDGE,"E220"),sQuery(id+"F0.wireOp",EDGE,"E221"),sQuery(id+"F0.wireOp",EDGE,"E222"),sQuery(id+"F0.wireOp",EDGE,"E223"),sQuery(id+"F0.wireOp",EDGE,"E224"),sQuery(id+"F0.wireOp",EDGE,"E225"),sQuery(id+"F0.wireOp",EDGE,"E226"),sQuery(id+"F0.wireOp",EDGE,"E227"),sQuery(id+"F0.wireOp",EDGE,"E228"),sQuery(id+"F0.wireOp",EDGE,"E229"),sQuery(id+"F0.wireOp",EDGE,"E230"),sQuery(id+"F0.wireOp",EDGE,"E231"),sQuery(id+"F0.wireOp",EDGE,"E232"),sQuery(id+"F0.wireOp",EDGE,"E233"),sQuery(id+"F0.wireOp",EDGE,"E234"),sQuery(id+"F0.wireOp",EDGE,"E235"),sQuery(id+"F0.wireOp",EDGE,"E236"),sQuery(id+"F0.wireOp",EDGE,"E237"),sQuery(id+"F0.wireOp",EDGE,"E238"),sQuery(id+"F0.wireOp",EDGE,"E239"),sQuery(id+"F0.wireOp",EDGE,"E240"),sQuery(id+"F0.wireOp",EDGE,"E241"),sQuery(id+"F0.wireOp",EDGE,"E242"),sQuery(id+"F0.wireOp",EDGE,"E243"),sQuery(id+"F0.wireOp",EDGE,"E244")])],"isStart":false});
            var sketch = newSketch(context, id + "F2", { "sketchPlane" : qUnion([Q0])});
            skText(sketch, "E245", { "text": "JANE", "fontName": "OpenSans-Bold.ttf"});
            const initialGuessF2  = {"E245": [-0.06628, 0.03645, 1, 0, 0.01336]};
            skSetInitialGuess(sketch, initialGuessF2);
            skSolve(sketch);
        }
        {
            var Q0;
            Q0 = qSketchRegion(id + "F2", true);
            extrude(context, id + "F3", {"entities" : qUnion([Q0]), "operationType" : NewBodyOperationType.ADD, "depth" : 2 * mm});
        }
        {
            var Q0;
            {var subQ0=sQuery(id+"F0.wireOp",EDGE,"E210");var subQ1=sQuery(id+"F0.wireOp",EDGE,"E209");var subQ2=sQuery(id+"F0.wireOp",EDGE,"E208");var subQ3=sQuery(id+"F0.wireOp",EDGE,"E207");var subQ4=sQuery(id+"F0.wireOp",EDGE,"E206");var subQ5=sQuery(id+"F0.wireOp",EDGE,"E205");var subQ6=sQuery(id+"F0.wireOp",EDGE,"E204");var subQ7=sQuery(id+"F0.wireOp",EDGE,"E203");var subQ8=sQuery(id+"F0.wireOp",EDGE,"E202");var subQ9=sQuery(id+"F0.wireOp",EDGE,"E201");var subQ10=sQuery(id+"F0.wireOp",EDGE,"E200");var subQ11=sQuery(id+"F0.wireOp",EDGE,"E199");var subQ12=sQuery(id+"F0.wireOp",EDGE,"E198");var subQ13=sQuery(id+"F0.wireOp",EDGE,"E197");var subQ14=sQuery(id+"F0.wireOp",EDGE,"E196");var subQ15=sQuery(id+"F0.wireOp",EDGE,"E195");var subQ16=sQuery(id+"F0.wireOp",EDGE,"E194");var subQ17=sQuery(id+"F0.wireOp",EDGE,"E193");var subQ18=sQuery(id+"F0.wireOp",EDGE,"E192");var subQ19=sQuery(id+"F0.wireOp",EDGE,"E191");var subQ20=sQuery(id+"F0.wireOp",EDGE,"E190");var subQ21=sQuery(id+"F0.wireOp",EDGE,"E189");var subQ22=sQuery(id+"F0.wireOp",EDGE,"E188");var subQ23=sQuery(id+"F0.wireOp",EDGE,"E187");var subQ24=sQuery(id+"F0.wireOp",EDGE,"E186");var subQ25=sQuery(id+"F0.wireOp",EDGE,"E185");var subQ26=sQuery(id+"F0.wireOp",EDGE,"E184");var subQ27=sQuery(id+"F0.wireOp",EDGE,"E183");var subQ28=sQuery(id+"F0.wireOp",EDGE,"E182");var subQ29=sQuery(id+"F0.wireOp",EDGE,"E181");var subQ30=sQuery(id+"F0.wireOp",EDGE,"E180");var subQ31=sQuery(id+"F0.wireOp",EDGE,"E179");var subQ32=sQuery(id+"F0.wireOp",EDGE,"E178");var subQ33=sQuery(id+"F0.wireOp",EDGE,"E177");var subQ34=sQuery(id+"F0.wireOp",EDGE,"E176");var subQ35=sQuery(id+"F0.wireOp",EDGE,"E175");var subQ36=sQuery(id+"F0.wireOp",EDGE,"E174");var subQ37=sQuery(id+"F0.wireOp",EDGE,"E173");var subQ38=sQuery(id+"F0.wireOp",EDGE,"E172");var subQ39=sQuery(id+"F0.wireOp",EDGE,"E171");var subQ40=sQuery(id+"F0.wireOp",EDGE,"E170");var subQ41=sQuery(id+"F0.wireOp",EDGE,"E169");var subQ42=sQuery(id+"F0.wireOp",EDGE,"E168");var subQ43=sQuery(id+"F0.wireOp",EDGE,"E167");var subQ44=sQuery(id+"F0.wireOp",EDGE,"E166");var subQ45=sQuery(id+"F0.wireOp",EDGE,"E165");var subQ46=sQuery(id+"F0.wireOp",EDGE,"E164");var subQ47=sQuery(id+"F0.wireOp",EDGE,"E163");var subQ48=sQuery(id+"F0.wireOp",EDGE,"E162");var subQ49=sQuery(id+"F0.wireOp",EDGE,"E161");var subQ50=sQuery(id+"F0.wireOp",EDGE,"E160");var subQ51=sQuery(id+"F0.wireOp",EDGE,"E159");var subQ52=sQuery(id+"F0.wireOp",EDGE,"E158");var subQ53=sQuery(id+"F0.wireOp",EDGE,"E157");var subQ54=sQuery(id+"F0.wireOp",EDGE,"E156");var subQ55=sQuery(id+"F0.wireOp",EDGE,"E155");var subQ56=sQuery(id+"F0.wireOp",EDGE,"E154");var subQ57=sQuery(id+"F0.wireOp",EDGE,"E153");var subQ58=sQuery(id+"F0.wireOp",EDGE,"E152");var subQ59=sQuery(id+"F0.wireOp",EDGE,"E151");var subQ60=sQuery(id+"F0.wireOp",EDGE,"E150");var subQ61=sQuery(id+"F0.wireOp",EDGE,"E149");var subQ62=sQuery(id+"F0.wireOp",EDGE,"E148");var subQ63=sQuery(id+"F0.wireOp",EDGE,"E147");var subQ64=sQuery(id+"F0.wireOp",EDGE,"E146");var subQ65=sQuery(id+"F0.wireOp",EDGE,"E145");var subQ66=sQuery(id+"F0.wireOp",EDGE,"E144");var subQ67=sQuery(id+"F0.wireOp",EDGE,"E143");var subQ68=sQuery(id+"F0.wireOp",EDGE,"E142");var subQ69=sQuery(id+"F0.wireOp",EDGE,"E141");var subQ70=sQuery(id+"F0.wireOp",EDGE,"E140");var subQ71=sQuery(id+"F0.wireOp",EDGE,"E139");var subQ72=sQuery(id+"F0.wireOp",EDGE,"E138");var subQ73=sQuery(id+"F0.wireOp",EDGE,"E137");var subQ74=sQuery(id+"F0.wireOp",EDGE,"E136");var subQ75=sQuery(id+"F0.wireOp",EDGE,"E135");var subQ76=sQuery(id+"F0.wireOp",EDGE,"E134");var subQ77=sQuery(id+"F0.wireOp",EDGE,"E133");var subQ78=sQuery(id+"F0.wireOp",EDGE,"E132");var subQ79=sQuery(id+"F0.wireOp",EDGE,"E131");var subQ80=sQuery(id+"F0.wireOp",EDGE,"E130");var subQ81=sQuery(id+"F0.wireOp",EDGE,"E129");var subQ82=sQuery(id+"F0.wireOp",EDGE,"E128");var subQ83=sQuery(id+"F0.wireOp",EDGE,"E127");var subQ84=sQuery(id+"F0.wireOp",EDGE,"E126");var subQ85=sQuery(id+"F0.wireOp",EDGE,"E125");var subQ86=sQuery(id+"F0.wireOp",EDGE,"E124");var subQ87=sQuery(id+"F0.wireOp",EDGE,"E123");var subQ88=sQuery(id+"F0.wireOp",EDGE,"E122");var subQ89=sQuery(id+"F0.wireOp",EDGE,"E121");var subQ90=sQuery(id+"F0.wireOp",EDGE,"E120");var subQ91=sQuery(id+"F0.wireOp",EDGE,"E119");var subQ92=sQuery(id+"F0.wireOp",EDGE,"E118");var subQ93=sQuery(id+"F0.wireOp",EDGE,"E117");var subQ94=sQuery(id+"F0.wireOp",EDGE,"E116");var subQ95=sQuery(id+"F0.wireOp",EDGE,"E115");var subQ96=sQuery(id+"F0.wireOp",EDGE,"E114");var subQ97=sQuery(id+"F0.wireOp",EDGE,"E113");var subQ98=sQuery(id+"F0.wireOp",EDGE,"E112");var subQ99=sQuery(id+"F0.wireOp",EDGE,"E111");var subQ100=sQuery(id+"F0.wireOp",EDGE,"E110");var subQ101=sQuery(id+"F0.wireOp",EDGE,"E109");var subQ102=sQuery(id+"F0.wireOp",EDGE,"E108");var subQ103=sQuery(id+"F0.wireOp",EDGE,"E107");var subQ104=sQuery(id+"F0.wireOp",EDGE,"E106");var subQ105=sQuery(id+"F0.wireOp",EDGE,"E105");var subQ106=sQuery(id+"F0.wireOp",EDGE,"E104");var subQ107=sQuery(id+"F0.wireOp",EDGE,"E103");var subQ108=sQuery(id+"F0.wireOp",EDGE,"E102");var subQ109=sQuery(id+"F0.wireOp",EDGE,"E101");var subQ110=sQuery(id+"F0.wireOp",EDGE,"E100");var subQ111=sQuery(id+"F0.wireOp",EDGE,"E99");var subQ112=sQuery(id+"F0.wireOp",EDGE,"E45");var subQ113=sQuery(id+"F0.wireOp",EDGE,"E44");var subQ114=sQuery(id+"F0.wireOp",EDGE,"E43");var subQ115=sQuery(id+"F0.wireOp",EDGE,"E42");var subQ116=sQuery(id+"F0.wireOp",EDGE,"E41");var subQ117=sQuery(id+"F0.wireOp",EDGE,"E40");var subQ118=sQuery(id+"F0.wireOp",EDGE,"E39");var subQ119=sQuery(id+"F0.wireOp",EDGE,"E38");var subQ120=sQuery(id+"F0.wireOp",EDGE,"E37");var subQ121=sQuery(id+"F0.wireOp",EDGE,"E36");var subQ122=sQuery(id+"F0.wireOp",EDGE,"E35");var subQ123=sQuery(id+"F0.wireOp",EDGE,"E34");var subQ124=sQuery(id+"F0.wireOp",EDGE,"E33");var subQ125=sQuery(id+"F0.wireOp",EDGE,"E32");var subQ126=sQuery(id+"F0.wireOp",EDGE,"E31");var subQ127=sQuery(id+"F0.wireOp",EDGE,"E30");var subQ128=sQuery(id+"F0.wireOp",EDGE,"E29");var subQ129=sQuery(id+"F0.wireOp",EDGE,"E28");var subQ130=sQuery(id+"F0.wireOp",EDGE,"E27");var subQ131=sQuery(id+"F0.wireOp",EDGE,"E26");var subQ132=sQuery(id+"F0.wireOp",EDGE,"E25");var subQ133=sQuery(id+"F0.wireOp",EDGE,"E24");var subQ134=sQuery(id+"F0.wireOp",EDGE,"E23");var subQ135=sQuery(id+"F0.wireOp",EDGE,"E22");var subQ136=sQuery(id+"F0.wireOp",EDGE,"E8");var subQ137=sQuery(id+"F0.wireOp",EDGE,"E7");var subQ138=sQuery(id+"F0.wireOp",EDGE,"E6");var subQ139=sQuery(id+"F0.wireOp",EDGE,"E5");var subQ140=sQuery(id+"F0.wireOp",EDGE,"E4");var subQ141=sQuery(id+"F0.wireOp",EDGE,"E9");var subQ142=sQuery(id+"F0.wireOp",EDGE,"E46");var subQ143=sQuery(id+"F0.wireOp",EDGE,"E211");var subQ144=sQuery(id+"F0.wireOp",EDGE,"E0");var subQ145=sQuery(id+"F0.wireOp",EDGE,"E98");var subQ146=sQuery(id+"F0.wireOp",EDGE,"E21");var subQ147=sQuery(id+"F0.wireOp",EDGE,"E3");var subQ148=sQuery(id+"F0.wireOp",EDGE,"E1");var subQ149=sQuery(id+"F0.wireOp",EDGE,"E2");var subQ150=sQuery(id+"F0.wireOp",EDGE,"E10");var subQ151=sQuery(id+"F0.wireOp",EDGE,"E11");var subQ152=sQuery(id+"F0.wireOp",EDGE,"E12");var subQ153=sQuery(id+"F0.wireOp",EDGE,"E13");var subQ154=sQuery(id+"F0.wireOp",EDGE,"E14");var subQ155=sQuery(id+"F0.wireOp",EDGE,"E15");var subQ156=sQuery(id+"F0.wireOp",EDGE,"E16");var subQ157=sQuery(id+"F0.wireOp",EDGE,"E17");var subQ158=sQuery(id+"F0.wireOp",EDGE,"E18");var subQ159=sQuery(id+"F0.wireOp",EDGE,"E19");var subQ160=sQuery(id+"F0.wireOp",EDGE,"E20");var subQ161=sQuery(id+"F0.wireOp",EDGE,"E47");var subQ162=sQuery(id+"F0.wireOp",EDGE,"E48");var subQ163=sQuery(id+"F0.wireOp",EDGE,"E49");var subQ164=sQuery(id+"F0.wireOp",EDGE,"E50");var subQ165=sQuery(id+"F0.wireOp",EDGE,"E51");var subQ166=sQuery(id+"F0.wireOp",EDGE,"E52");var subQ167=sQuery(id+"F0.wireOp",EDGE,"E53");var subQ168=sQuery(id+"F0.wireOp",EDGE,"E54");var subQ169=sQuery(id+"F0.wireOp",EDGE,"E55");var subQ170=sQuery(id+"F0.wireOp",EDGE,"E56");var subQ171=sQuery(id+"F0.wireOp",EDGE,"E57");var subQ172=sQuery(id+"F0.wireOp",EDGE,"E58");var subQ173=sQuery(id+"F0.wireOp",EDGE,"E59");var subQ174=sQuery(id+"F0.wireOp",EDGE,"E60");var subQ175=sQuery(id+"F0.wireOp",EDGE,"E61");var subQ176=sQuery(id+"F0.wireOp",EDGE,"E62");var subQ177=sQuery(id+"F0.wireOp",EDGE,"E63");var subQ178=sQuery(id+"F0.wireOp",EDGE,"E64");var subQ179=sQuery(id+"F0.wireOp",EDGE,"E65");var subQ180=sQuery(id+"F0.wireOp",EDGE,"E66");var subQ181=sQuery(id+"F0.wireOp",EDGE,"E67");var subQ182=sQuery(id+"F0.wireOp",EDGE,"E68");var subQ183=sQuery(id+"F0.wireOp",EDGE,"E69");var subQ184=sQuery(id+"F0.wireOp",EDGE,"E70");var subQ185=sQuery(id+"F0.wireOp",EDGE,"E71");var subQ186=sQuery(id+"F0.wireOp",EDGE,"E72");var subQ187=sQuery(id+"F0.wireOp",EDGE,"E73");var subQ188=sQuery(id+"F0.wireOp",EDGE,"E74");var subQ189=sQuery(id+"F0.wireOp",EDGE,"E75");var subQ190=sQuery(id+"F0.wireOp",EDGE,"E76");var subQ191=sQuery(id+"F0.wireOp",EDGE,"E77");var subQ192=sQuery(id+"F0.wireOp",EDGE,"E78");var subQ193=sQuery(id+"F0.wireOp",EDGE,"E80");var subQ194=sQuery(id+"F0.wireOp",EDGE,"E79");var subQ195=sQuery(id+"F0.wireOp",EDGE,"E81");var subQ196=sQuery(id+"F0.wireOp",EDGE,"E82");var subQ197=sQuery(id+"F0.wireOp",EDGE,"E83");var subQ198=sQuery(id+"F0.wireOp",EDGE,"E84");var subQ199=sQuery(id+"F0.wireOp",EDGE,"E85");var subQ200=sQuery(id+"F0.wireOp",EDGE,"E86");var subQ201=sQuery(id+"F0.wireOp",EDGE,"E87");var subQ202=sQuery(id+"F0.wireOp",EDGE,"E88");var subQ203=sQuery(id+"F0.wireOp",EDGE,"E89");var subQ204=sQuery(id+"F0.wireOp",EDGE,"E90");var subQ205=sQuery(id+"F0.wireOp",EDGE,"E91");var subQ206=sQuery(id+"F0.wireOp",EDGE,"E93");var subQ207=sQuery(id+"F0.wireOp",EDGE,"E92");var subQ208=sQuery(id+"F0.wireOp",EDGE,"E94");var subQ209=sQuery(id+"F0.wireOp",EDGE,"E95");var subQ210=sQuery(id+"F0.wireOp",EDGE,"E96");var subQ211=sQuery(id+"F0.wireOp",EDGE,"E97");var subQ212=sQuery(id+"F0.wireOp",EDGE,"E213");var subQ213=sQuery(id+"F0.wireOp",EDGE,"E212");var subQ214=sQuery(id+"F0.wireOp",EDGE,"E214");var subQ215=sQuery(id+"F0.wireOp",EDGE,"E215");var subQ216=sQuery(id+"F0.wireOp",EDGE,"E217");var subQ217=sQuery(id+"F0.wireOp",EDGE,"E216");var subQ218=sQuery(id+"F0.wireOp",EDGE,"E218");var subQ219=sQuery(id+"F0.wireOp",EDGE,"E219");var subQ220=sQuery(id+"F0.wireOp",EDGE,"E220");var subQ221=sQuery(id+"F0.wireOp",EDGE,"E221");var subQ222=sQuery(id+"F0.wireOp",EDGE,"E222");var subQ223=sQuery(id+"F0.wireOp",EDGE,"E223");var subQ224=sQuery(id+"F0.wireOp",EDGE,"E224");var subQ225=sQuery(id+"F0.wireOp",EDGE,"E225");var subQ226=sQuery(id+"F0.wireOp",EDGE,"E226");var subQ227=sQuery(id+"F0.wireOp",EDGE,"E227");var subQ228=sQuery(id+"F0.wireOp",EDGE,"E228");var subQ229=sQuery(id+"F0.wireOp",EDGE,"E229");var subQ230=sQuery(id+"F0.wireOp",EDGE,"E231");var subQ231=sQuery(id+"F0.wireOp",EDGE,"E230");var subQ232=sQuery(id+"F0.wireOp",EDGE,"E232");var subQ233=sQuery(id+"F0.wireOp",EDGE,"E233");var subQ234=sQuery(id+"F0.wireOp",EDGE,"E234");var subQ235=sQuery(id+"F0.wireOp",EDGE,"E235");var subQ236=sQuery(id+"F0.wireOp",EDGE,"E236");var subQ237=sQuery(id+"F0.wireOp",EDGE,"E237");var subQ238=sQuery(id+"F0.wireOp",EDGE,"E238");var subQ239=sQuery(id+"F0.wireOp",EDGE,"E239");var subQ240=sQuery(id+"F0.wireOp",EDGE,"E240");var subQ241=sQuery(id+"F0.wireOp",EDGE,"E241");var subQ242=sQuery(id+"F0.wireOp",EDGE,"E242");var subQ243=sQuery(id+"F0.wireOp",EDGE,"E243");var subQ244=sQuery(id+"F0.wireOp",EDGE,"E244");Q0=makeQuery(id+"F3.boolean.opBoolean","SPLIT",FACE,{"disambiguationData":[TD([makeQuery(id+"F1.opExtrude","SWEPT_FACE",FACE,{"disambiguationData":[OSD([subQ144])]})])],"derivedFrom":makeQuery(id+"F1.opExtrude","CAP_FACE",FACE,{"disambiguationData":[OSD([subQ144,subQ148,subQ149,subQ147,subQ140,subQ139,subQ138,subQ137,subQ136,subQ141,subQ150,subQ151,subQ152,subQ153,subQ154,subQ155,subQ156,subQ157,subQ158,subQ159,subQ160,subQ146,subQ135,subQ134,subQ133,subQ132,subQ131,subQ130,subQ129,subQ128,subQ127,subQ126,subQ125,subQ124,subQ123,subQ122,subQ121,subQ120,subQ119,subQ118,subQ117,subQ116,subQ115,subQ114,subQ113,subQ112,subQ142,subQ161,subQ162,subQ163,subQ164,subQ165,subQ166,subQ167,subQ168,subQ169,subQ170,subQ171,subQ172,subQ173,subQ174,subQ175,subQ176,subQ177,subQ178,subQ179,subQ180,subQ181,subQ182,subQ183,subQ184,subQ185,subQ186,subQ187,subQ188,subQ189,subQ190,subQ191,subQ192,subQ194,subQ193,subQ195,subQ196,subQ197,subQ198,subQ199,subQ200,subQ201,subQ202,subQ203,subQ204,subQ205,subQ207,subQ206,subQ208,subQ209,subQ210,subQ211,subQ145,subQ111,subQ110,subQ109,subQ108,subQ107,subQ106,subQ105,subQ104,subQ103,subQ102,subQ101,subQ100,subQ99,subQ98,subQ97,subQ96,subQ95,subQ94,subQ93,subQ92,subQ91,subQ90,subQ89,subQ88,subQ87,subQ86,subQ85,subQ84,subQ83,subQ82,subQ81,subQ80,subQ79,subQ78,subQ77,subQ76,subQ75,subQ74,subQ73,subQ72,subQ71,subQ70,subQ69,subQ68,subQ67,subQ66,subQ65,subQ64,subQ63,subQ62,subQ61,subQ60,subQ59,subQ58,subQ57,subQ56,subQ55,subQ54,subQ53,subQ52,subQ51,subQ50,subQ49,subQ48,subQ47,subQ46,subQ45,subQ44,subQ43,subQ42,subQ41,subQ40,subQ39,subQ38,subQ37,subQ36,subQ35,subQ34,subQ33,subQ32,subQ31,subQ30,subQ29,subQ28,subQ27,subQ26,subQ25,subQ24,subQ23,subQ22,subQ21,subQ20,subQ19,subQ18,subQ17,subQ16,subQ15,subQ14,subQ13,subQ12,subQ11,subQ10,subQ9,subQ8,subQ7,subQ6,subQ5,subQ4,subQ3,subQ2,subQ1,subQ0,subQ143,subQ213,subQ212,subQ214,subQ215,subQ217,subQ216,subQ218,subQ219,subQ220,subQ221,subQ222,subQ223,subQ224,subQ225,subQ226,subQ227,subQ228,subQ229,subQ231,subQ230,subQ232,subQ233,subQ234,subQ235,subQ236,subQ237,subQ238,subQ239,subQ240,subQ241,subQ242,subQ243,subQ244])],"isStart":false})});}
            var sketch = newSketch(context, id + "F4", { "sketchPlane" : qUnion([Q0])});
            skCircle(sketch, "E246", {"center": v(-69.52, 65.7) * mm, "radius": 2.75 * mm});
            skSolve(sketch);
        }
        {
            var Q0;
            Q0 = qSketchRegion(id + "F4", true);
            extrude(context, id + "F5", {"entities" : qUnion([Q0]), "operationType" : NewBodyOperationType.REMOVE, "oppositeDirection" : true, "depth" : 25 * mm});
        }
    });
